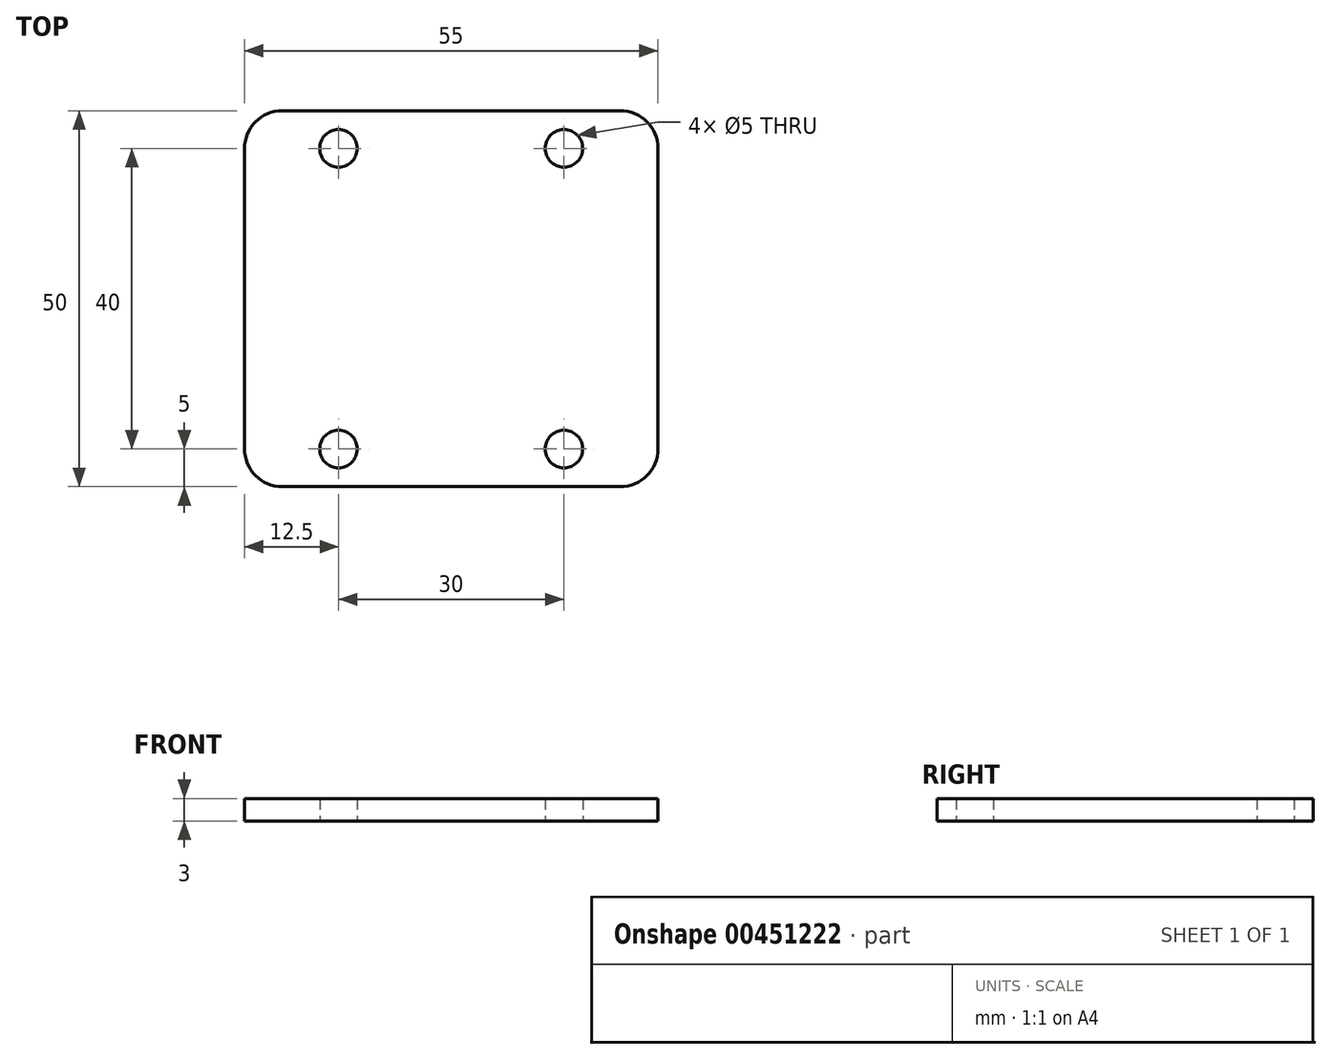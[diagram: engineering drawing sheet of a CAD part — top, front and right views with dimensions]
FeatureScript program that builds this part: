
annotation { "Feature Type Name" : "Feature", "Feature Type Description" : "" }
export const myFeature = defineFeature(function(context is Context, id is Id, definition is map)
    precondition{}
    {
        {
            var Q0;
            Q0=qCreatedBy(makeId("Top.planeOp"),FACE);
            var sketch = newSketch(context, id + "F0", { "sketchPlane" : qUnion([Q0])});
            skLineSegment(sketch, "E0.bottom", {"start": v(27.5, -25) * mm, "end": v(-27.5, -25) * mm});
            skLineSegment(sketch, "E0.top", {"start": v(27.5, 25) * mm, "end": v(-27.5, 25) * mm});
            skLineSegment(sketch, "E0.left", {"start": v(27.5, -25) * mm, "end": v(27.5, 25) * mm});
            skLineSegment(sketch, "E0.right", {"start": v(-27.5, -25) * mm, "end": v(-27.5, 25) * mm});
            skPoint(sketch, "E0.middle", {"position": v(0, 0) * mm});
            skCircle(sketch, "E1", {"center": v(-15, 20) * mm, "radius": 2.5 * mm});
            skCircle(sketch, "E2", {"center": v(15, 20) * mm, "radius": 2.5 * mm});
            skCircle(sketch, "E3", {"center": v(-15, -20) * mm, "radius": 2.5 * mm});
            skCircle(sketch, "E4", {"center": v(15, -20) * mm, "radius": 2.5 * mm});
            skSolve(sketch);
        }
        {
            var Q0;
            Q0=qSketchRegion(id+"F0",true);
            extrude(context, id + "F1", {"entities" : qUnion([Q0]), "depth" : 3 * mm, "offsetDistance" : 25 * mm});
        }
        {
            var Q0;
            Q0=makeQuery(id+"F1.opExtrude","SWEPT_EDGE",EDGE,{"disambiguationData":[OSD([sQuery(id+"F0.wireOp",EDGE,"E0.top"),sQuery(id+"F0.wireOp",EDGE,"E0.right")])]});
            var Q1;
            Q1=makeQuery(id+"F1.opExtrude","SWEPT_EDGE",EDGE,{"disambiguationData":[OSD([sQuery(id+"F0.wireOp",EDGE,"E0.top"),sQuery(id+"F0.wireOp",EDGE,"E0.left")])]});
            var Q2;
            Q2=makeQuery(id+"F1.opExtrude","SWEPT_EDGE",EDGE,{"disambiguationData":[OSD([sQuery(id+"F0.wireOp",EDGE,"E0.bottom"),sQuery(id+"F0.wireOp",EDGE,"E0.right")])]});
            var Q3;
            Q3=makeQuery(id+"F1.opExtrude","SWEPT_EDGE",EDGE,{"disambiguationData":[OSD([sQuery(id+"F0.wireOp",EDGE,"E0.bottom"),sQuery(id+"F0.wireOp",EDGE,"E0.left")])]});
            fillet(context, id + "F2", {"entities" : qUnion([Q0, Q1, Q2, Q3]), "tangentPropagation" : true, "radius" : 5 * mm, "defaultsChanged" : false, "vertexSettings" : [], "allowEdgeOverflow" : false});
        }
    });
